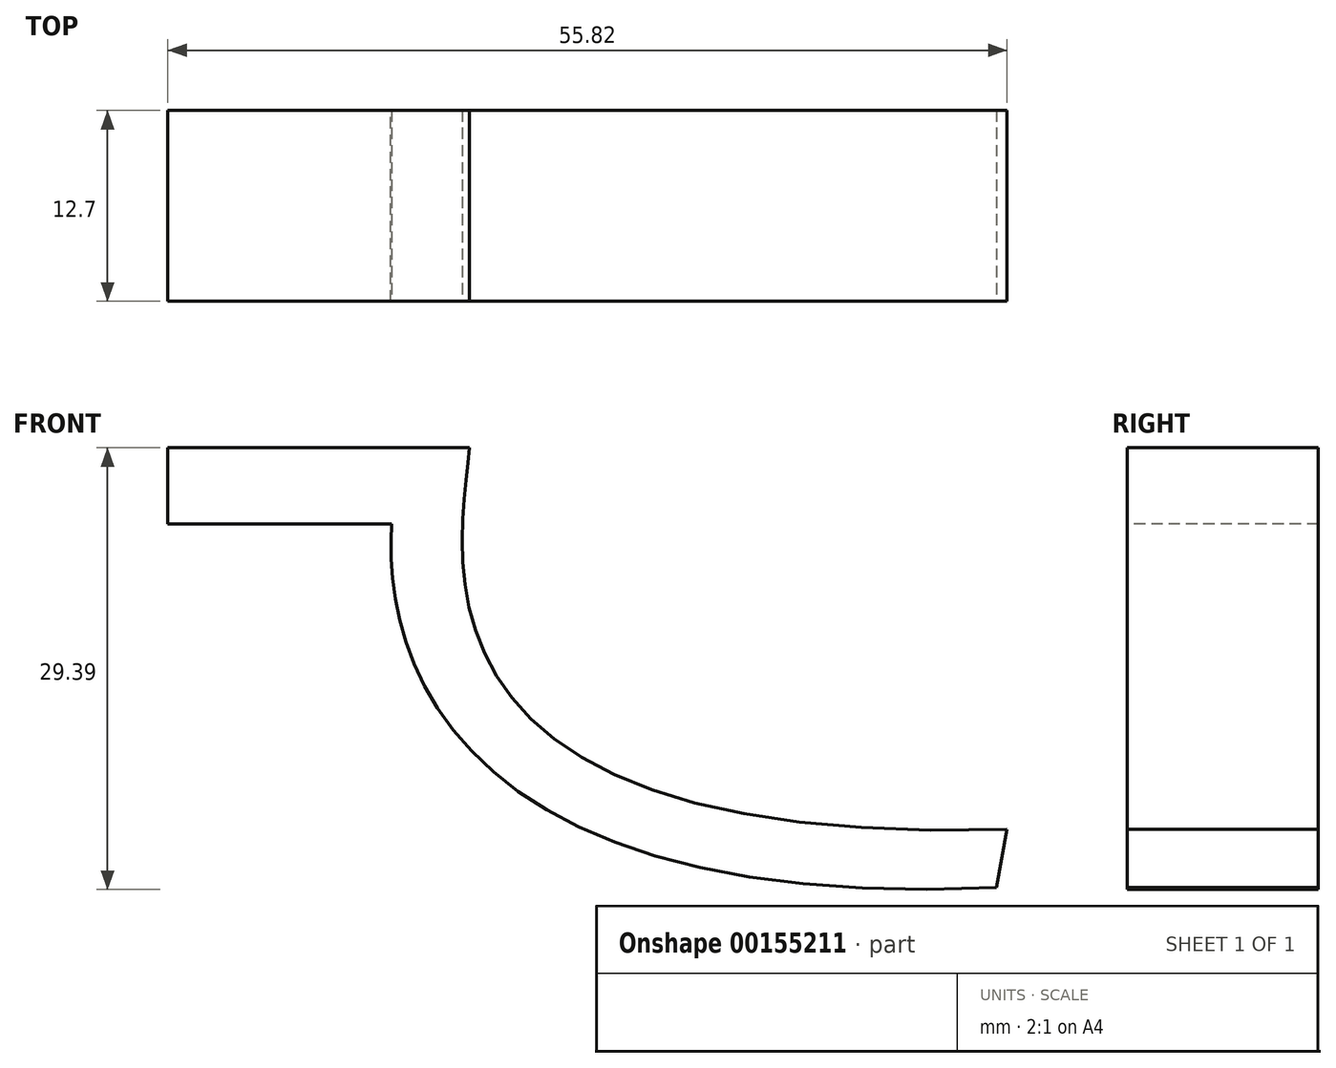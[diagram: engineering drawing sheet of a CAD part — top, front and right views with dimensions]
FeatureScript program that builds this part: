
annotation { "Feature Type Name" : "Feature", "Feature Type Description" : "" }
export const myFeature = defineFeature(function(context is Context, id is Id, definition is map)
    precondition{}
    {
        {
            var Q0;
            Q0=qCreatedBy(makeId("Front.planeOp"),FACE);
            var sketch = newSketch(context, id + "F0", { "sketchPlane" : qUnion([Q0])});
            skLineSegment(sketch, "E0", {"start": v(-51.7, 35.82) * mm, "end": v(-31.64, 35.82) * mm});
            skFitSpline(sketch, "E1", {"points": [v(-31.64, 35.82) * mm, v(4.12, 10.42) * mm], "startDerivative": vector(-2, -22.06) * mm, "endDerivative": vector(122.78, 3.74) * mm});
            skLineSegment(sketch, "E2", {"start": v(-51.7, 35.82) * mm, "end": v(-51.7, 30.74) * mm});
            skLineSegment(sketch, "E3", {"start": v(-51.7, 30.74) * mm, "end": v(-36.81, 30.74) * mm});
            skFitSpline(sketch, "E4", {"points": [v(-36.81, 30.74) * mm, v(3.4, 6.55) * mm], "startDerivative": vector(-1.75, -24.48) * mm, "endDerivative": vector(111.04, 5.25) * mm});
            skLineSegment(sketch, "E5", {"start": v(3.4, 6.55) * mm, "end": v(4.12, 10.42) * mm});
            skSolve(sketch);
        }
        {
            var Q0;
            Q0 = qSketchRegion(id + "F0", true);
            extrude(context, id + "F1", {"entities" : qUnion([Q0]), "oppositeDirection" : true, "depth" : 12.7 * mm});
        }
    });
